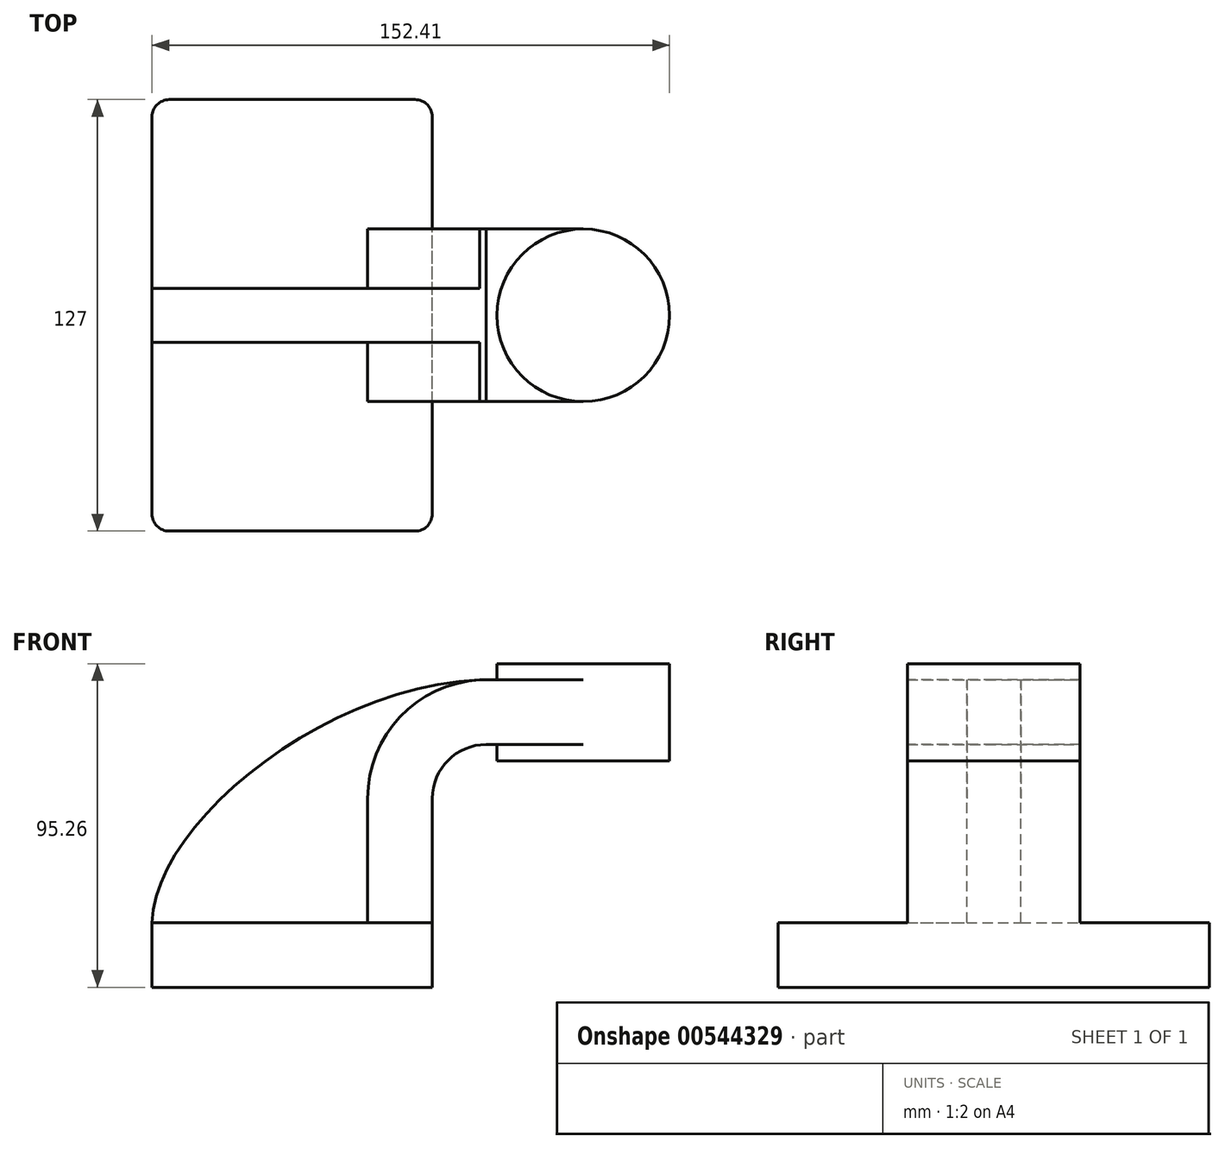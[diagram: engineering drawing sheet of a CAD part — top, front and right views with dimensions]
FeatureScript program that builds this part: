
annotation { "Feature Type Name" : "Feature", "Feature Type Description" : "" }
export const myFeature = defineFeature(function(context is Context, id is Id, definition is map)
    precondition{}
    {
        {
            var Q0;
            Q0=qCreatedBy(makeId("Front.planeOp"),FACE);
            var sketch = newSketch(context, id + "F0", { "sketchPlane" : qUnion([Q0])});
            skLineSegment(sketch, "E0.bottom", {"start": v(41.28, -9.52) * mm, "end": v(-41.28, -9.53) * mm});
            skLineSegment(sketch, "E0.top", {"start": v(41.28, 9.53) * mm, "end": v(-41.28, 9.53) * mm});
            skLineSegment(sketch, "E0.left", {"start": v(41.28, -9.52) * mm, "end": v(41.28, 9.53) * mm});
            skLineSegment(sketch, "E0.right", {"start": v(-41.28, -9.53) * mm, "end": v(-41.28, 9.53) * mm});
            skPoint(sketch, "E0.middle", {"position": v(0, 0) * mm});
            skLineSegment(sketch, "E1.bottom", {"start": v(111.12, 57.15) * mm, "end": v(60.33, 57.15) * mm});
            skLineSegment(sketch, "E1.top", {"start": v(111.12, 85.73) * mm, "end": v(60.33, 85.73) * mm});
            skLineSegment(sketch, "E1.left", {"start": v(111.12, 57.15) * mm, "end": v(111.12, 85.73) * mm});
            skLineSegment(sketch, "E1.right", {"start": v(60.33, 57.15) * mm, "end": v(60.33, 85.73) * mm});
            skPoint(sketch, "E1.middle", {"position": v(85.72, 71.44) * mm});
            skLineSegment(sketch, "E2", {"start": v(41.28, 9.53) * mm, "end": v(41.28, 46.05) * mm});
            skArc(sketch, "E3", {"start": v(41.27, 46.05) * mm, "mid": v(45.92, 57.28) * mm, "end": v(57.15, 61.93) * mm});
            skLineSegment(sketch, "E4", {"start": v(57.15, 61.93) * mm, "end": v(85.72, 61.93) * mm});
            skLineSegment(sketch, "E5.0", {"start": v(57.15, 80.98) * mm, "end": v(85.72, 80.98) * mm});
            skArc(sketch, "E5.1", {"start": v(22.23, 46.05) * mm, "mid": v(32.45, 70.75) * mm, "end": v(57.15, 80.98) * mm});
            skLineSegment(sketch, "E5.2", {"start": v(22.22, 9.53) * mm, "end": v(22.22, 46.05) * mm});
            skLineSegment(sketch, "E6", {"start": v(85.72, 57.15) * mm, "end": v(85.72, 85.73) * mm});
            skFitSpline(sketch, "E7", {"points": [v(-41.28, 9.52) * mm, v(57.15, 80.98) * mm], "startDerivative": vector(1.85, 86.67) * mm, "endDerivative": vector(142, 2.34) * mm});
            skSolve(sketch);
        }
        {
            var Q0;
            Q0=makeQuery(id+"F0.imprint","IMPRINT",FACE,{"disambiguationData":[TD([[makeQuery(id+"F0.imprint","IMPRINT",EDGE,{"derivedFrom":sQuery(id+"F0.wireOp",EDGE,"E0.bottom")}),-1.0]])]});
            extrude(context, id + "F1", {"entities" : qUnion([Q0]), "endBound" : BoundingType.SYMMETRIC, "depth" : 127 * mm, "offsetDistance" : 25.4 * mm});
        }
        {
            var Q0;
            {var subQ1=sQuery(id+"F0.wireOp",EDGE,"E2");Q0=makeQuery(id+"F0.imprint","IMPRINT",FACE,{"disambiguationData":[TD([[makeQuery(id+"F0.imprint","IMPRINT",EDGE,{"derivedFrom":subQ1}),1.0]])]});}
            var Q1;
            {var subQ0=sQuery(id+"F0.wireOp",EDGE,"E4");var subQ1=sQuery(id+"F0.wireOp",EDGE,"E1.right");var subQ2=makeQuery(id+"F0.imprint","INTERSECT",VERTEX,{"derivedFrom":[subQ1,subQ0]});Q1=makeQuery(id+"F0.imprint","IMPRINT",FACE,{"disambiguationData":[TD([[makeQuery(id+"F0.imprint","IMPRINT",EDGE,{"disambiguationData":[TD([[subQ2,-1.0]])],"derivedFrom":subQ1}),-1.0]])]});}
            extrude(context, id + "F2", {"entities" : qUnion([Q0, Q1]), "operationType" : NewBodyOperationType.ADD, "endBound" : BoundingType.SYMMETRIC, "depth" : 50.8 * mm, "offsetDistance" : 25.4 * mm});
        }
        {
            var Q0;
            {var subQ3=sQuery(id+"F0.wireOp",EDGE,"E5.2");Q0=makeQuery(id+"F0.imprint","IMPRINT",FACE,{"disambiguationData":[TD([[makeQuery(id+"F0.imprint","IMPRINT",EDGE,{"derivedFrom":subQ3}),1.0]])]});}
            extrude(context, id + "F3", {"entities" : qUnion([Q0]), "operationType" : NewBodyOperationType.ADD, "endBound" : BoundingType.SYMMETRIC, "depth" : 15.88 * mm, "offsetDistance" : 25.4 * mm});
        }
        {
            var Q0;
            {var subQ0=sQuery(id+"F0.wireOp",EDGE,"E1.left");Q0=makeQuery(id+"F0.imprint","IMPRINT",FACE,{"disambiguationData":[TD([[makeQuery(id+"F0.imprint","IMPRINT",EDGE,{"derivedFrom":subQ0}),1.0]])]});}
            var Q1;
            Q1=sQuery(id+"F0.wireOp",EDGE,"E6");
            revolve(context, id + "F4", {"operationType" : NewBodyOperationType.ADD, "entities" : qUnion([Q0]), "axis" : qUnion([Q1]), "revolveType" : RevolveType.FULL});
        }
        {
            var Q0;
            Q0=makeQuery(id+"F1.opExtrude","CAP_EDGE",EDGE,{"disambiguationData":[OSD([sQuery(id+"F0.wireOp",EDGE,"E0.left")])],"isStart":false});
            var Q1;
            Q1=makeQuery(id+"F1.opExtrude","CAP_EDGE",EDGE,{"disambiguationData":[OSD([sQuery(id+"F0.wireOp",EDGE,"E0.right")])],"isStart":false});
            var Q2;
            Q2=makeQuery(id+"F1.opExtrude","CAP_EDGE",EDGE,{"disambiguationData":[OSD([sQuery(id+"F0.wireOp",EDGE,"E0.left")])],"isStart":true});
            var Q3;
            Q3=makeQuery(id+"F1.opExtrude","CAP_EDGE",EDGE,{"disambiguationData":[OSD([sQuery(id+"F0.wireOp",EDGE,"E0.right")])],"isStart":true});
            fillet(context, id + "F5", {"entities" : qUnion([Q0, Q1, Q2, Q3]), "radius" : 5.08 * mm, "tangentPropagation" : true, "allowEdgeOverflow" : false});
        }
    });
